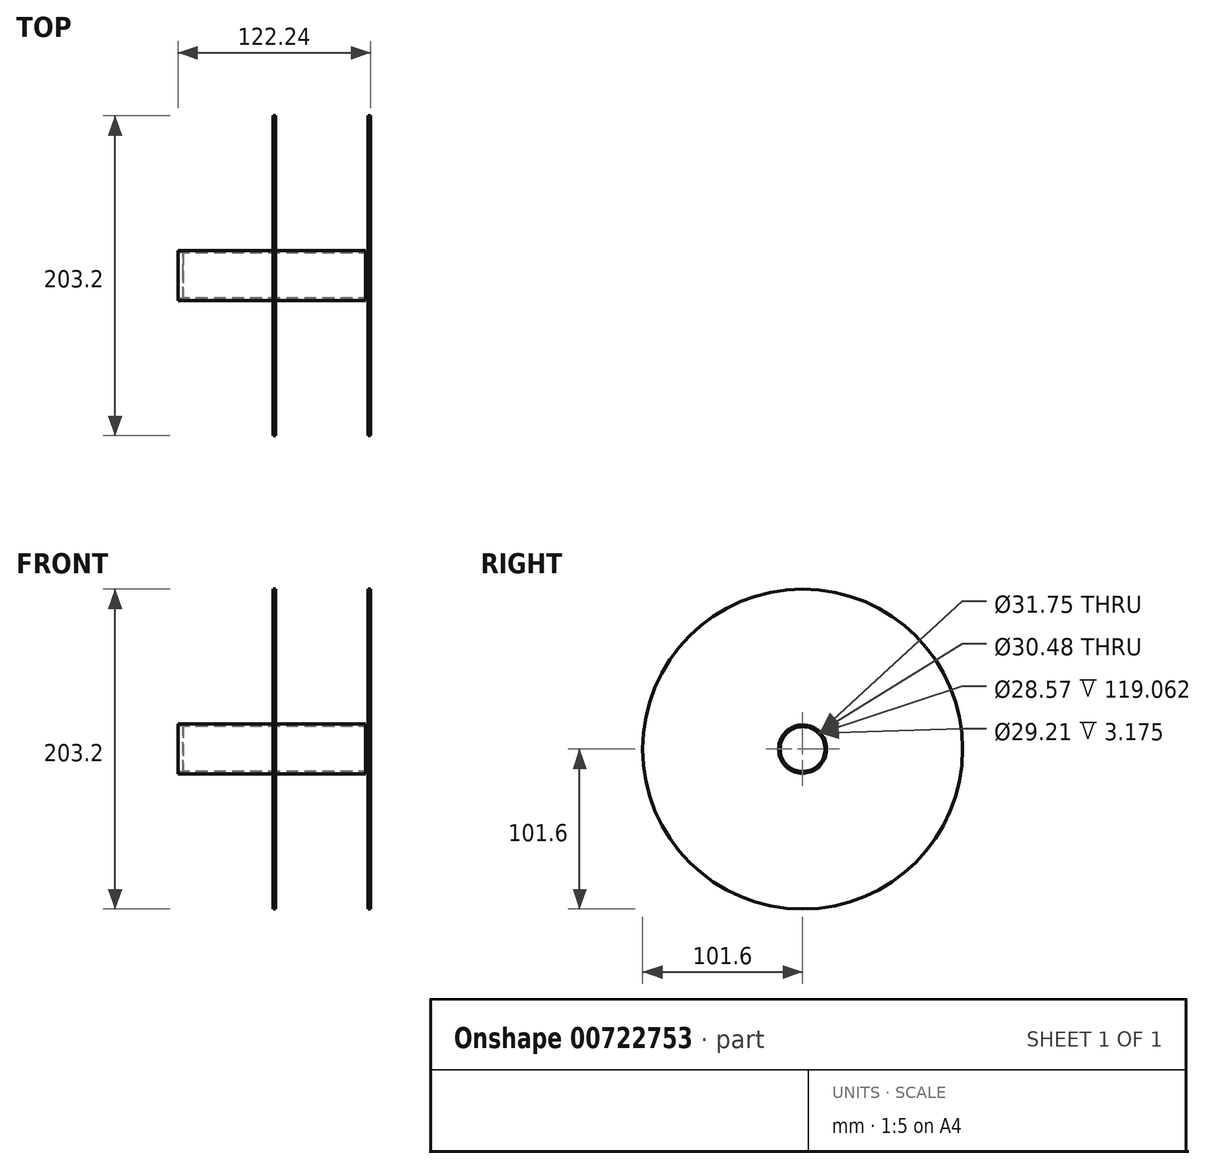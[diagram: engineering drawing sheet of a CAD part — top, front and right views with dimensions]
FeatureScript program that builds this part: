
annotation { "Feature Type Name" : "Feature", "Feature Type Description" : "" }
export const myFeature = defineFeature(function(context is Context, id is Id, definition is map)
    precondition{}
    {
        {
            var Q0;
            Q0=qCreatedBy(makeId("Right.planeOp"),FACE);
            var sketch = newSketch(context, id + "F0", { "sketchPlane" : qUnion([Q0])});
            skCircle(sketch, "E0", {"center": v(0, 0) * mm, "radius": 15.88 * mm});
            skCircle(sketch, "E1", {"center": v(0, 0) * mm, "radius": 14.29 * mm});
            skCircle(sketch, "E2", {"center": v(0, 0) * mm, "radius": 14.6 * mm});
            skSolve(sketch);
        }
        {
            var Q0;
            Q0=makeQuery(id+"F0.imprint","IMPRINT",FACE,{"disambiguationData":[TD([[makeQuery(id+"F0.imprint","IMPRINT",EDGE,{"derivedFrom":sQuery(id+"F0.wireOp",EDGE,"E1")}),-1.0]])]});
            var Q1;
            Q1=makeQuery(id+"F0.imprint","IMPRINT",FACE,{"disambiguationData":[TD([[makeQuery(id+"F0.imprint","IMPRINT",EDGE,{"derivedFrom":sQuery(id+"F0.wireOp",EDGE,"E0")}),1.0]])]});
            extrude(context, id + "F1", {"entities" : qUnion([Q0, Q1]), "endBound" : BoundingType.SYMMETRIC, "depth" : 122.24 * mm, "offsetDistance" : 25.4 * mm});
        }
        {
            var Q0;
            Q0=makeQuery(id+"F1.opExtrude","CAP_FACE",FACE,{"disambiguationData":[OSD([sQuery(id+"F0.wireOp",EDGE,"E0"),sQuery(id+"F0.wireOp",EDGE,"E1")])],"isStart":false});
            var sketch = newSketch(context, id + "F2", { "sketchPlane" : qUnion([Q0])});
            skCircle(sketch, "E3.0", {"center": v(0, 0) * mm, "radius": 14.6 * mm});
            skSolve(sketch);
        }
        {
            var Q0;
            Q0=makeQuery(id+"F2.imprint","IMPRINT",FACE,{"disambiguationData":[TD([[makeQuery(id+"F2.imprint","IMPRINT",EDGE,{"derivedFrom":sQuery(id+"F2.wireOp",EDGE,"E3.0")}),-1.0]])]});
            extrude(context, id + "F3", {"entities" : qUnion([Q0]), "operationType" : NewBodyOperationType.REMOVE, "oppositeDirection" : true, "depth" : 3.17 * mm, "offsetDistance" : 25.4 * mm});
        }
        {
            var Q0;
            Q0=makeQuery(id+"F1.opExtrude","CAP_FACE",FACE,{"disambiguationData":[OSD([sQuery(id+"F0.wireOp",EDGE,"E0"),sQuery(id+"F0.wireOp",EDGE,"E1")])],"isStart":true});
            var sketch = newSketch(context, id + "F4", { "sketchPlane" : qUnion([Q0])});
            skCircle(sketch, "E4.0", {"center": v(0, 0) * mm, "radius": 14.6 * mm});
            skSolve(sketch);
        }
        {
            var Q0;
            Q0=makeQuery(id+"F4.imprint","IMPRINT",FACE,{"disambiguationData":[TD([[makeQuery(id+"F4.imprint","IMPRINT",EDGE,{"derivedFrom":sQuery(id+"F4.wireOp",EDGE,"E4.0")}),1.0]])]});
            extrude(context, id + "F5", {"entities" : qUnion([Q0]), "operationType" : NewBodyOperationType.REMOVE, "oppositeDirection" : true, "depth" : 3.17 * mm, "offsetDistance" : 25.4 * mm});
        }
        {
            var Q0;
            Q0=makeQuery(id+"F1.opExtrude","CAP_FACE",FACE,{"disambiguationData":[OSD([sQuery(id+"F0.wireOp",EDGE,"E0"),sQuery(id+"F0.wireOp",EDGE,"E1")])],"isStart":false});
            var sketch = newSketch(context, id + "F6", { "sketchPlane" : qUnion([Q0])});
            skCircle(sketch, "E5", {"center": v(0, 0) * mm, "radius": 15.24 * mm});
            skCircle(sketch, "E6", {"center": v(0, 0) * mm, "radius": 101.6 * mm});
            skSolve(sketch);
        }
        {
            var Q0;
            Q0 = qSketchRegion(id + "F6", true);
            extrude(context, id + "F7", {"entities" : qUnion([Q0]), "oppositeDirection" : true, "depth" : 1.59 * mm, "offsetDistance" : 25.4 * mm});
        }
        {
            var Q0;
            Q0=qCreatedBy(makeId("Right.planeOp"),FACE);
            var sketch = newSketch(context, id + "F8", { "sketchPlane" : qUnion([Q0])});
            skCircle(sketch, "E7.0", {"center": v(0, 0) * mm, "radius": 15.88 * mm});
            skCircle(sketch, "E8", {"center": v(0, 0) * mm, "radius": 101.6 * mm});
            skSolve(sketch);
        }
        {
            var Q0;
            Q0 = qSketchRegion(id + "F8", true);
            extrude(context, id + "F9", {"entities" : qUnion([Q0]), "endBound" : BoundingType.SYMMETRIC, "depth" : 1.59 * mm, "offsetDistance" : 25.4 * mm});
        }
    });
